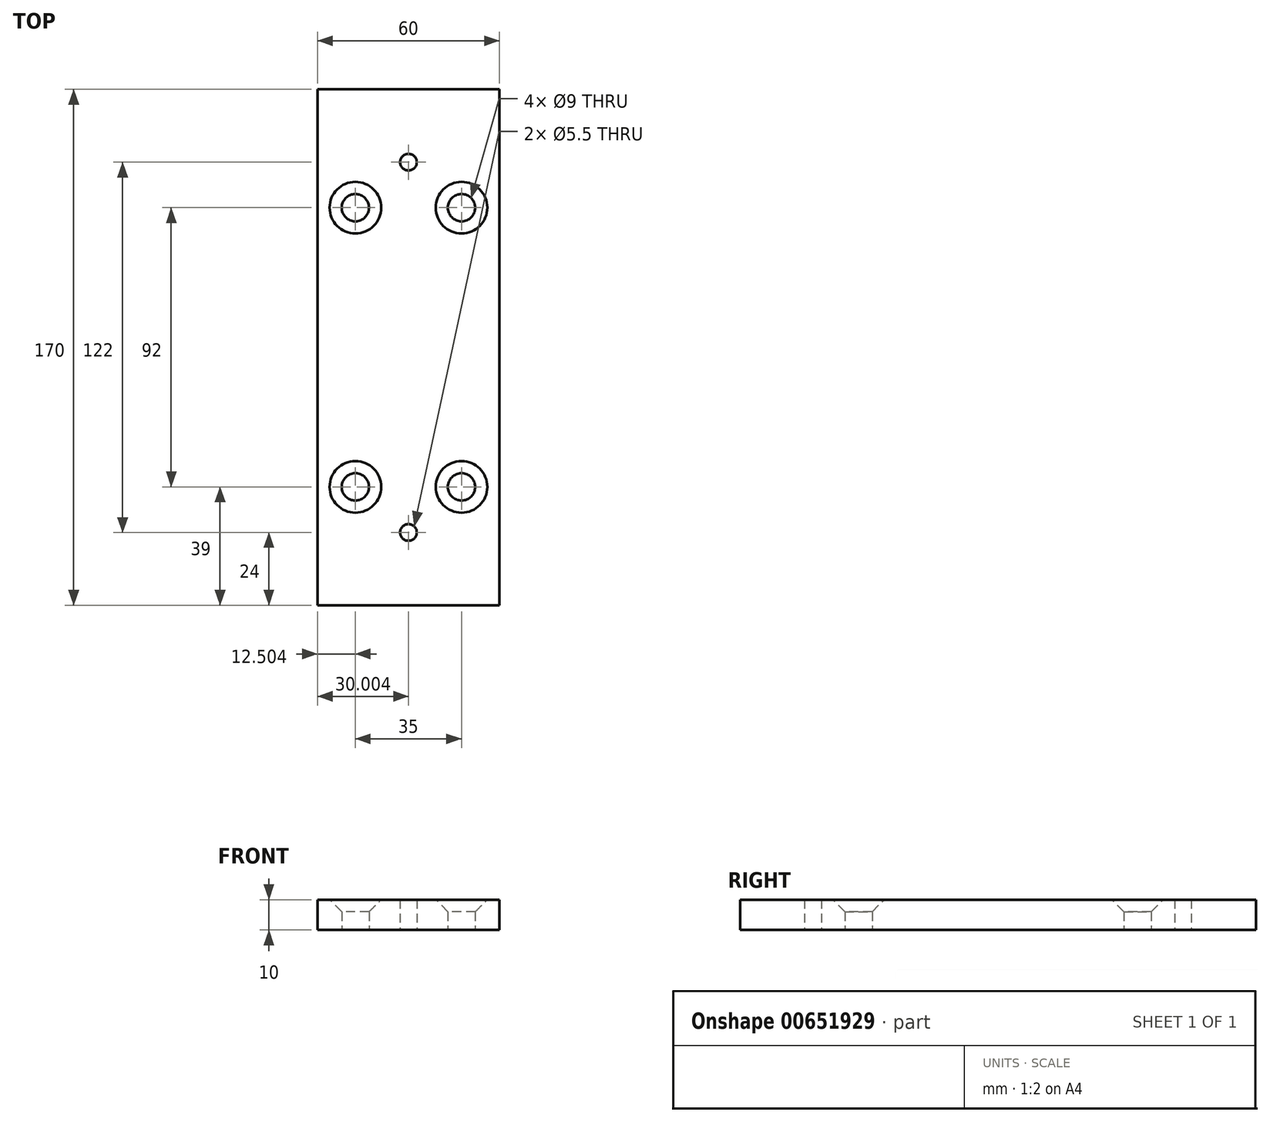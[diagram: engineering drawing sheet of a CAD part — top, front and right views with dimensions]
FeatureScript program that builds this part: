
annotation { "Feature Type Name" : "Feature", "Feature Type Description" : "" }
export const myFeature = defineFeature(function(context is Context, id is Id, definition is map)
    precondition{}
    {
        {
            var Q0;
            Q0=qCreatedBy(makeId("Top.planeOp"),FACE);
            var sketch = newSketch(context, id + "F0", { "sketchPlane" : qUnion([Q0])});
            skLineSegment(sketch, "E0.bottom", {"start": v(27.22, 0) * mm, "end": v(-32.78, 0) * mm});
            skLineSegment(sketch, "E0.top", {"start": v(27.22, 170) * mm, "end": v(-32.78, 170) * mm});
            skLineSegment(sketch, "E0.left", {"start": v(27.22, 0) * mm, "end": v(27.22, 170) * mm});
            skLineSegment(sketch, "E0.right", {"start": v(-32.78, 0) * mm, "end": v(-32.78, 170) * mm});
            skCircle(sketch, "E1", {"center": v(-20.28, 39) * mm, "radius": 4.5 * mm});
            skCircle(sketch, "E2", {"center": v(14.72, 39) * mm, "radius": 4.5 * mm});
            skCircle(sketch, "E3", {"center": v(-20.28, 131) * mm, "radius": 4.5 * mm});
            skCircle(sketch, "E4", {"center": v(14.72, 131) * mm, "radius": 4.5 * mm});
            skCircle(sketch, "E5", {"center": v(-2.78, 24) * mm, "radius": 2.75 * mm});
            skCircle(sketch, "E6", {"center": v(-2.78, 146) * mm, "radius": 2.75 * mm});
            skSolve(sketch);
        }
        {
            var Q0;
            Q0=makeQuery(id+"F0.imprint","IMPRINT",FACE,{"disambiguationData":[TD([[makeQuery(id+"F0.imprint","IMPRINT",EDGE,{"derivedFrom":sQuery(id+"F0.wireOp",EDGE,"E0.bottom")}),-1.0]])]});
            extrude(context, id + "F1", {"entities" : qUnion([Q0]), "depth" : 10 * mm, "offsetDistance" : 25 * mm});
        }
        {
            var Q0;
            Q0=makeQuery(id+"F1.opExtrude","CAP_EDGE",EDGE,{"disambiguationData":[OSD([sQuery(id+"F0.wireOp",EDGE,"E1")])],"isStart":false});
            var Q1;
            Q1=makeQuery(id+"F1.opExtrude","CAP_EDGE",EDGE,{"disambiguationData":[OSD([sQuery(id+"F0.wireOp",EDGE,"E2")])],"isStart":false});
            var Q2;
            Q2=makeQuery(id+"F1.opExtrude","CAP_EDGE",EDGE,{"disambiguationData":[OSD([sQuery(id+"F0.wireOp",EDGE,"E4")])],"isStart":false});
            var Q3;
            Q3=makeQuery(id+"F1.opExtrude","CAP_EDGE",EDGE,{"disambiguationData":[OSD([sQuery(id+"F0.wireOp",EDGE,"E3")])],"isStart":false});
            chamfer(context, id + "F2", {"entities" : qUnion([Q0, Q1, Q2, Q3]), "width" : 4 * mm, "tangentPropagation" : true});
        }
    });
